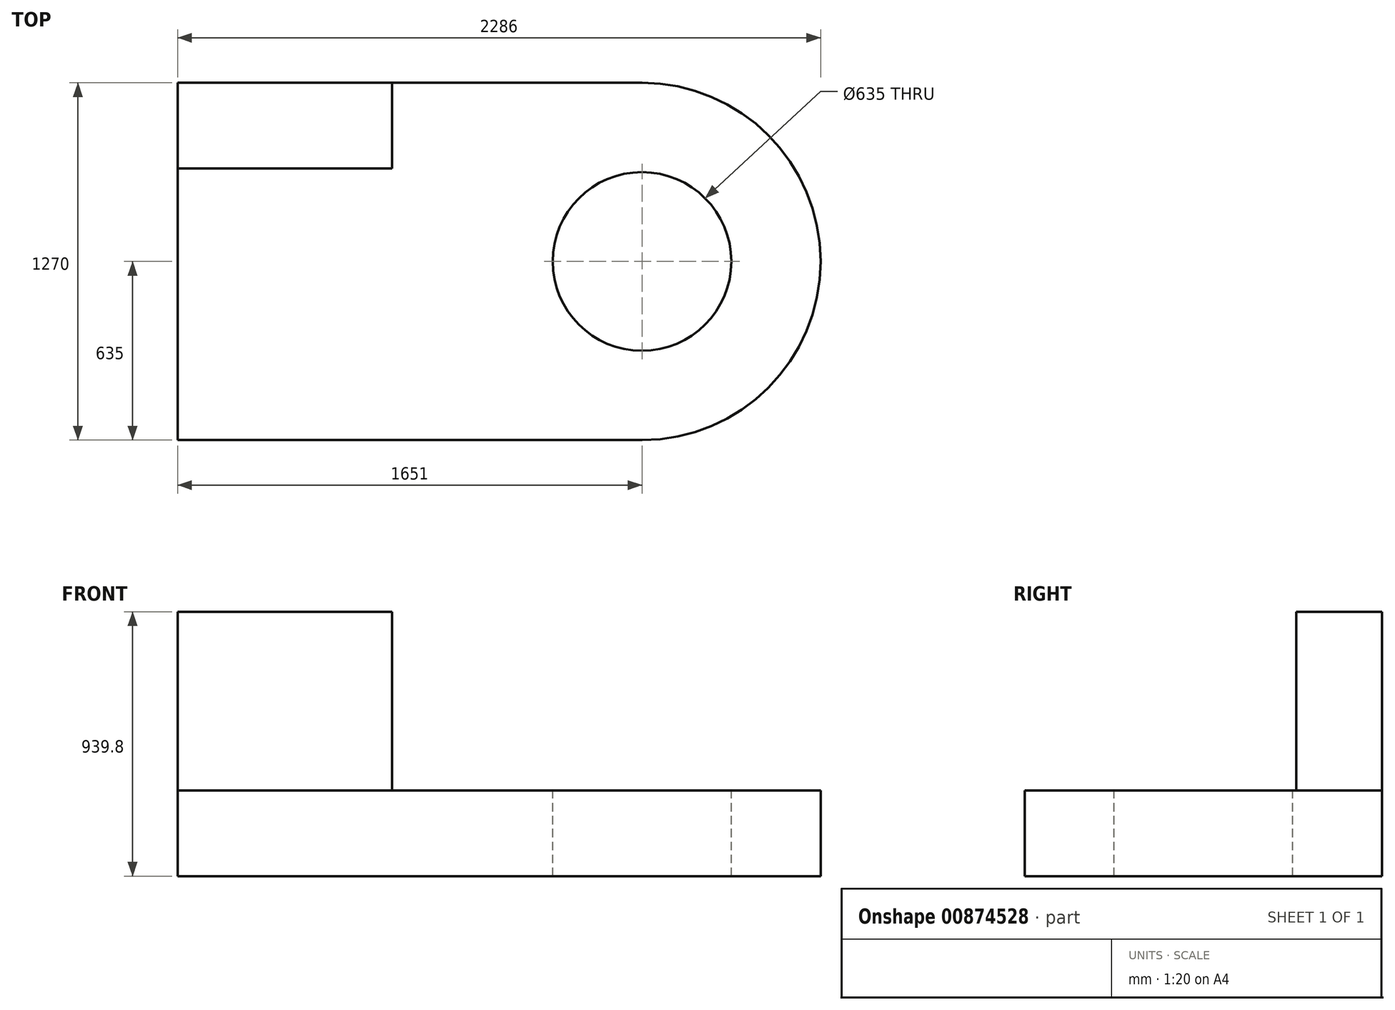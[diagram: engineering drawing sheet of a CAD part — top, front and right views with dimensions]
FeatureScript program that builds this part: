
annotation { "Feature Type Name" : "Feature", "Feature Type Description" : "" }
export const myFeature = defineFeature(function(context is Context, id is Id, definition is map)
    precondition{}
    {
        {
            var Q0;
            Q0=qCreatedBy(makeId("Top.planeOp"),FACE);
            var sketch = newSketch(context, id + "F0", { "sketchPlane" : qUnion([Q0])});
            skLineSegment(sketch, "E0.bottom", {"start": v(0, 0) * mm, "end": v(-1651, 0) * mm});
            skLineSegment(sketch, "E0.top", {"start": v(0, -1270) * mm, "end": v(-1651, -1270) * mm});
            skLineSegment(sketch, "E0.left", {"start": v(0, 0) * mm, "end": v(0, -1270) * mm});
            skLineSegment(sketch, "E0.right", {"start": v(-1651, 0) * mm, "end": v(-1651, -1270) * mm});
            skSolve(sketch);
        }
        {
            var Q0;
            Q0 = qSketchRegion(id + "F0", true);
            extrude(context, id + "F1", {"entities" : qUnion([Q0]), "depth" : 304.8 * mm, "offsetDistance" : 25.4 * mm});
        }
        {
            var Q0;
            Q0=makeQuery(id+"F1.opExtrude","CAP_FACE",FACE,{"disambiguationData":[OSD([sQuery(id+"F0.wireOp",EDGE,"E0.bottom"),sQuery(id+"F0.wireOp",EDGE,"E0.top"),sQuery(id+"F0.wireOp",EDGE,"E0.left"),sQuery(id+"F0.wireOp",EDGE,"E0.right")])],"isStart":false});
            var sketch = newSketch(context, id + "F2", { "sketchPlane" : qUnion([Q0])});
            skLineSegment(sketch, "E1.bottom", {"start": v(-1651, 0) * mm, "end": v(-889, 0) * mm});
            skLineSegment(sketch, "E1.top", {"start": v(-1651, -304.8) * mm, "end": v(-889, -304.8) * mm});
            skLineSegment(sketch, "E1.left", {"start": v(-1651, 0) * mm, "end": v(-1651, -304.8) * mm});
            skLineSegment(sketch, "E1.right", {"start": v(-889, 0) * mm, "end": v(-889, -304.8) * mm});
            skSolve(sketch);
        }
        {
            var Q0;
            Q0 = qSketchRegion(id + "F2", true);
            extrude(context, id + "F3", {"entities" : qUnion([Q0]), "operationType" : NewBodyOperationType.ADD, "depth" : 635 * mm, "offsetDistance" : 25.4 * mm});
        }
        {
            var Q0;
            Q0=makeQuery(id+"F1.opExtrude","CAP_FACE",FACE,{"disambiguationData":[OSD([sQuery(id+"F0.wireOp",EDGE,"E0.bottom"),sQuery(id+"F0.wireOp",EDGE,"E0.top"),sQuery(id+"F0.wireOp",EDGE,"E0.left"),sQuery(id+"F0.wireOp",EDGE,"E0.right")])],"isStart":false});
            var sketch = newSketch(context, id + "F4", { "sketchPlane" : qUnion([Q0])});
            skCircle(sketch, "E2", {"center": v(0, -635) * mm, "radius": 635 * mm});
            skSolve(sketch);
        }
        {
            var Q0;
            {var subQ1=makeQuery(id+"F1.opExtrude","CAP_EDGE",EDGE,{"disambiguationData":[OSD([sQuery(id+"F0.wireOp",EDGE,"E0.left")])],"isStart":false});Q0=makeQuery(id+"F4.imprint","IMPRINT",FACE,{"disambiguationData":[TD([[makeQuery(id+"F4.imprint","IMPRINT",EDGE,{"derivedFrom":subQ1}),1.0]])]});}
            extrude(context, id + "F5", {"entities" : qUnion([Q0]), "operationType" : NewBodyOperationType.ADD, "oppositeDirection" : true, "depth" : 304.8 * mm, "offsetDistance" : 25.4 * mm});
        }
        {
            var Q0;
            {var subQ0=sQuery(id+"F0.wireOp",EDGE,"E0.left");Q0=makeQuery(id+"F5.boolean.opBoolean","MERGE",FACE,{"derivedFrom":[makeQuery(id+"F1.opExtrude","CAP_FACE",FACE,{"disambiguationData":[OSD([sQuery(id+"F0.wireOp",EDGE,"E0.bottom"),sQuery(id+"F0.wireOp",EDGE,"E0.top"),subQ0,sQuery(id+"F0.wireOp",EDGE,"E0.right")])],"isStart":false}),makeQuery(id+"F5.opExtrude","CAP_FACE",FACE,{"disambiguationData":[OSD([subQ0,sQuery(id+"F4.wireOp",EDGE,"E2")])],"isStart":true})]});}
            var sketch = newSketch(context, id + "F6", { "sketchPlane" : qUnion([Q0])});
            skLineSegment(sketch, "E3", {"start": v(0, -1270) * mm, "end": v(0, 0) * mm});
            skCircle(sketch, "E4", {"center": v(0, -635) * mm, "radius": 317.5 * mm});
            skSolve(sketch);
        }
        {
            var Q0;
            Q0 = qSketchRegion(id + "F6", true);
            extrude(context, id + "F7", {"entities" : qUnion([Q0]), "operationType" : NewBodyOperationType.REMOVE, "oppositeDirection" : true, "depth" : 304.8 * mm, "offsetDistance" : 25.4 * mm});
        }
    });
